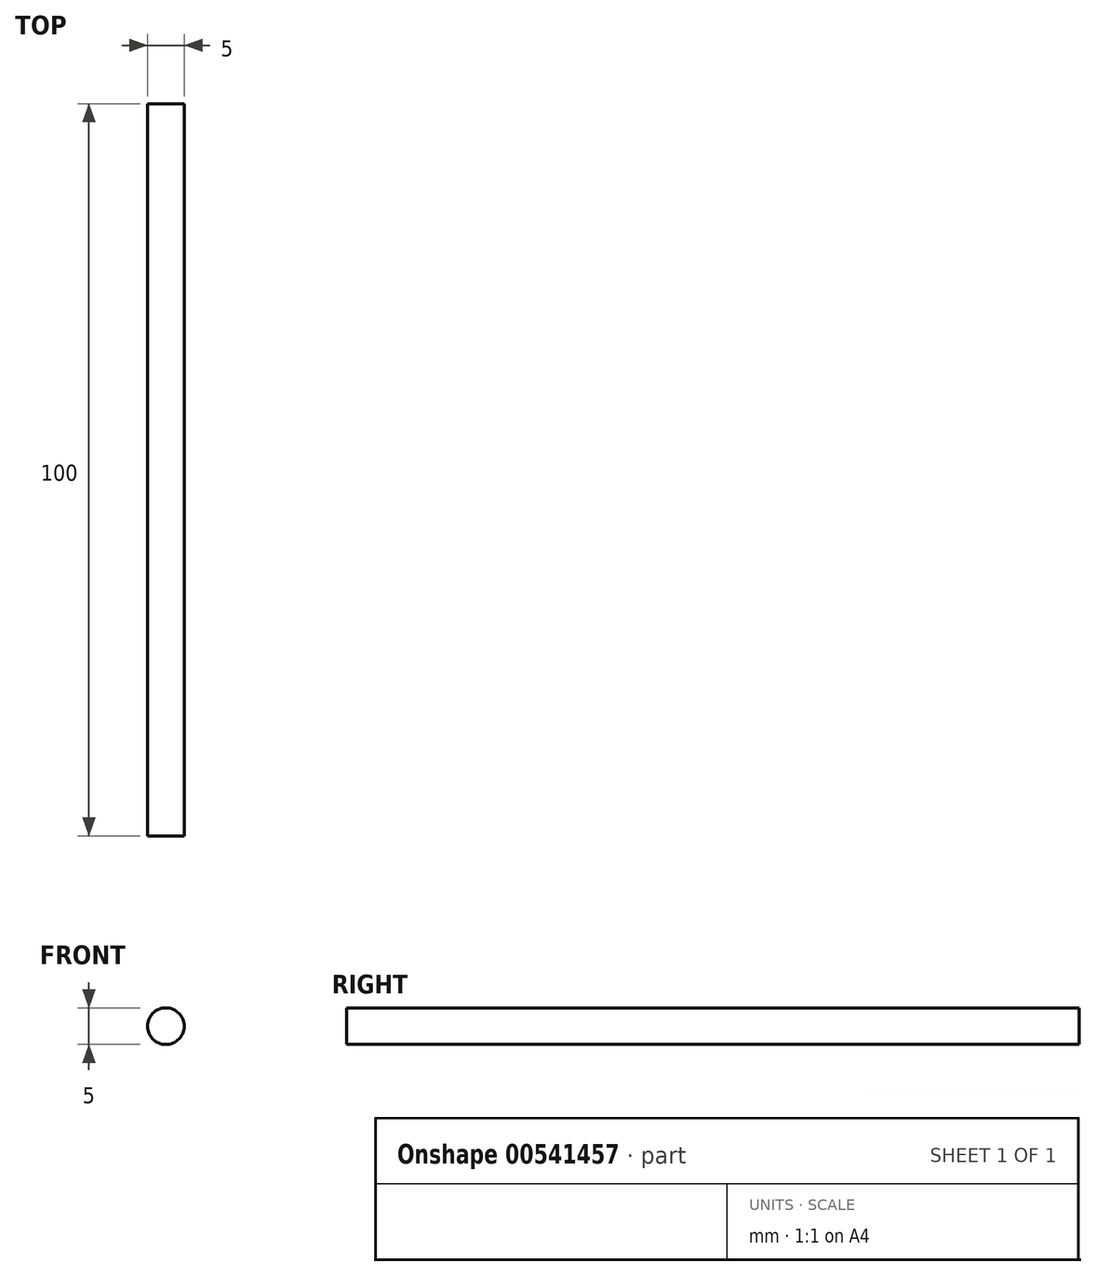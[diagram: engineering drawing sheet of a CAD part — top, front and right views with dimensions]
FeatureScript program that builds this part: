
annotation { "Feature Type Name" : "Feature", "Feature Type Description" : "" }
export const myFeature = defineFeature(function(context is Context, id is Id, definition is map)
    precondition{}
    {
        {
            var Q0;
            Q0=qCreatedBy(makeId("Front.planeOp"),FACE);
            var sketch = newSketch(context, id + "F0", { "sketchPlane" : qUnion([Q0])});
            skCircle(sketch, "E0", {"center": v(0, 0) * mm, "radius": 2.5 * mm});
            skSolve(sketch);
        }
        {
            var Q0;
            Q0=makeQuery(id+"F0.imprint","IMPRINT",FACE,{"disambiguationData":[TD([[makeQuery(id+"F0.imprint","IMPRINT",EDGE,{"derivedFrom":sQuery(id+"F0.wireOp",EDGE,"E0")}),1.0]])]});
            extrude(context, id + "F1", {"entities" : qUnion([Q0]), "depth" : 100 * mm, "offsetDistance" : 25.4 * mm});
        }
    });
